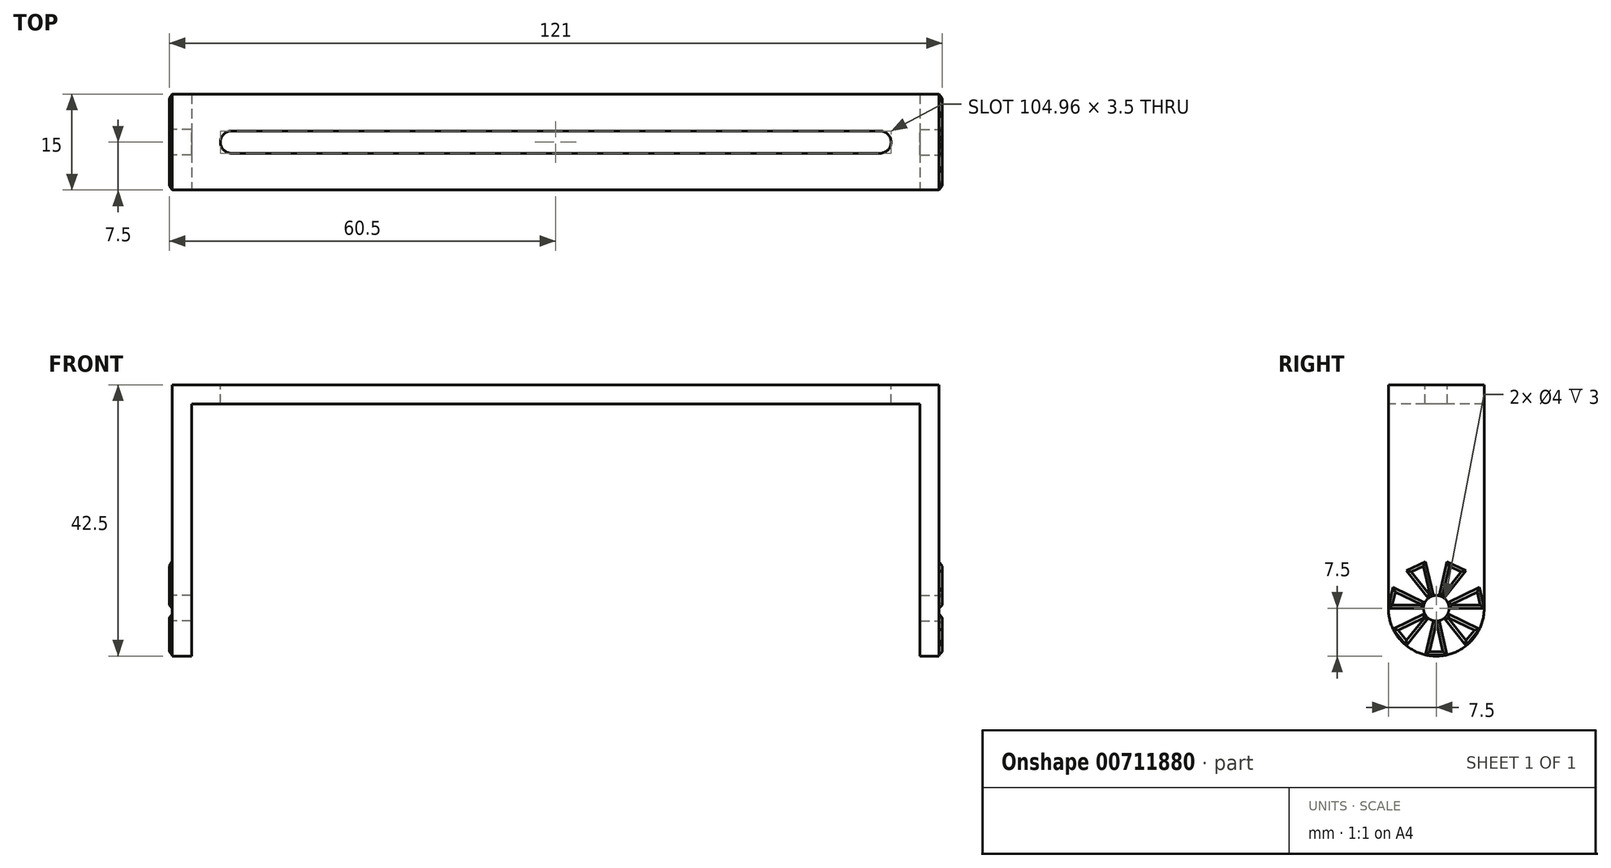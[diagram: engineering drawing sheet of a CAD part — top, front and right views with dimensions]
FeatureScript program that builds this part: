
annotation { "Feature Type Name" : "Feature", "Feature Type Description" : "" }
export const myFeature = defineFeature(function(context is Context, id is Id, definition is map)
    precondition{}
    {
        {
            var Q0;
            Q0=qCreatedBy(makeId("Top.planeOp"),FACE);
            var sketch = newSketch(context, id + "F0", { "sketchPlane" : qUnion([Q0])});
            skLineSegment(sketch, "E0", {"start": v(0, 7.5) * mm, "end": v(0, -7.5) * mm});
            skLineSegment(sketch, "E1", {"start": v(0, 7.5) * mm, "end": v(-60, 7.5) * mm});
            skLineSegment(sketch, "E2", {"start": v(-60, 7.5) * mm, "end": v(-60, -7.5) * mm});
            skLineSegment(sketch, "E3", {"start": v(0, -7.5) * mm, "end": v(-60, -7.5) * mm});
            skLineSegment(sketch, "E4", {"start": v(-57, 7.5) * mm, "end": v(-57, -7.5) * mm});
            skLineSegment(sketch, "E5.trimOffspring", {"start": v(-55, 0) * mm, "end": v(-50.73, 0) * mm});
            skPoint(sketch, "E6.start.orphan", {"position": v(-60, 0) * mm});
            skPoint(sketch, "E7.end.orphan", {"position": v(0, -3.5) * mm});
            skPoint(sketch, "E7.start.orphan", {"position": v(-60.73, -3.5) * mm});
            skPoint(sketch, "E8.end.orphan", {"position": v(-60.8, -3.5) * mm});
            skPoint(sketch, "E9.end.orphan", {"position": v(0, 3.5) * mm});
            skLineSegment(sketch, "E10", {"start": v(-50.73, 0) * mm, "end": v(0, 0) * mm});
            skPoint(sketch, "E11.orphan", {"position": v(-57, 0) * mm});
            skArc(sketch, "E12.0.startCap", {"start": v(-50.73, -1.75) * mm, "mid": v(-52.48, 0) * mm, "end": v(-50.73, 1.75) * mm});
            skLineSegment(sketch, "E12.0.left", {"start": v(-50.73, 1.75) * mm, "end": v(10, 1.75) * mm});
            skLineSegment(sketch, "E12.0.right", {"start": v(-50.73, -1.75) * mm, "end": v(10, -1.75) * mm});
            skSolve(sketch);
        }
        {
            var Q0;
            {var subQ0=sQuery(id+"F0.wireOp",EDGE,"E2");Q0=makeQuery(id+"F0.imprint","IMPRINT",FACE,{"disambiguationData":[TD([[makeQuery(id+"F0.imprint","IMPRINT",EDGE,{"derivedFrom":subQ0}),1.0]])]});}
            extrude(context, id + "F1", {"entities" : qUnion([Q0]), "oppositeDirection" : true, "depth" : 35 * mm, "offsetDistance" : 25 * mm});
        }
        {
            var Q0;
            {var subQ3=sQuery(id+"F0.wireOp",EDGE,"E4");Q0=makeQuery(id+"F0.imprint","IMPRINT",FACE,{"disambiguationData":[TD([[makeQuery(id+"F0.imprint","IMPRINT",EDGE,{"derivedFrom":subQ3}),1.0]])]});}
            extrude(context, id + "F2", {"entities" : qUnion([Q0]), "operationType" : NewBodyOperationType.ADD, "oppositeDirection" : true, "depth" : 3 * mm, "offsetDistance" : 25 * mm});
        }
        {
            var Q0;
            Q0=makeQuery(id+"F1.opExtrude","CAP_FACE",FACE,{"disambiguationData":[OSD([sQuery(id+"F0.wireOp",EDGE,"E1"),sQuery(id+"F0.wireOp",EDGE,"E2"),sQuery(id+"F0.wireOp",EDGE,"E3"),sQuery(id+"F0.wireOp",EDGE,"E4")])],"isStart":false});
            var sketch = newSketch(context, id + "F3", { "sketchPlane" : qUnion([Q0])});
            skLineSegment(sketch, "E13", {"start": v(-74.84, 0) * mm, "end": v(-34.44, 0) * mm});
            skPoint(sketch, "E13.startSnap0", {"position": v(-60, 0) * mm});
            skSolve(sketch);
        }
        {
            var Q0;
            {var subQ5=makeQuery(id+"F1.opExtrude","CAP_EDGE",EDGE,{"disambiguationData":[OSD([sQuery(id+"F0.wireOp",EDGE,"E3")])],"isStart":false});Q0=makeQuery(id+"F3.imprint","IMPRINT",FACE,{"disambiguationData":[TD([[makeQuery(id+"F3.imprint","IMPRINT",EDGE,{"derivedFrom":subQ5}),1.0]])]});}
            var Q1;
            Q1=sQuery(id+"F3.wireOp",EDGE,"E13");
            revolve(context, id + "F4", {"operationType" : NewBodyOperationType.ADD, "surfaceOperationType" : NewSurfaceOperationType.NEW, "entities" : qUnion([Q0]), "axis" : qUnion([Q1]), "revolveType" : RevolveType.FULL});
        }
        {
            var Q0;
            {var subQ0=sQuery(id+"F0.wireOp",EDGE,"E2");Q0=makeQuery(id+"F4.boolean.opBoolean","MERGE",FACE,{"derivedFrom":[makeQuery(id+"F1.opExtrude","SWEPT_FACE",FACE,{"disambiguationData":[OSD([subQ0])]}),makeQuery(id+"F4.opRevolve","SWEPT_FACE",FACE,{"disambiguationData":[OSD([subQ0])]})]});}
            var sketch = newSketch(context, id + "F5", { "sketchPlane" : qUnion([Q0])});
            skCircle(sketch, "E14", {"center": v(0, -35) * mm, "radius": 7.5 * mm});
            skCircle(sketch, "E15", {"center": v(0, -35) * mm, "radius": 2 * mm});
            skCircle(sketch, "E16.cCircle", {"center": v(0, -35) * mm, "radius": 7.5 * mm, "construction": true});
            skLineSegment(sketch, "E16.0", {"start": v(7.5, -35) * mm, "end": v(6.76, -38.25) * mm});
            skLineSegment(sketch, "E16.1", {"start": v(6.76, -38.25) * mm, "end": v(4.68, -40.86) * mm});
            skLineSegment(sketch, "E16.2", {"start": v(4.68, -40.86) * mm, "end": v(1.67, -42.31) * mm});
            skLineSegment(sketch, "E16.3", {"start": v(1.67, -42.31) * mm, "end": v(-1.67, -42.31) * mm});
            skLineSegment(sketch, "E16.4", {"start": v(-1.67, -42.31) * mm, "end": v(-4.68, -40.86) * mm});
            skLineSegment(sketch, "E16.5", {"start": v(-4.68, -40.86) * mm, "end": v(-6.76, -38.25) * mm});
            skLineSegment(sketch, "E16.6", {"start": v(-6.76, -38.25) * mm, "end": v(-7.5, -35) * mm});
            skLineSegment(sketch, "E16.7", {"start": v(-7.5, -35) * mm, "end": v(-6.76, -31.75) * mm});
            skLineSegment(sketch, "E16.8", {"start": v(-6.76, -31.75) * mm, "end": v(-4.68, -29.14) * mm});
            skLineSegment(sketch, "E16.9", {"start": v(-4.68, -29.14) * mm, "end": v(-1.67, -27.69) * mm});
            skLineSegment(sketch, "E16.10", {"start": v(-1.67, -27.69) * mm, "end": v(1.67, -27.69) * mm});
            skLineSegment(sketch, "E16.11", {"start": v(1.67, -27.69) * mm, "end": v(4.68, -29.14) * mm});
            skLineSegment(sketch, "E16.12", {"start": v(4.68, -29.14) * mm, "end": v(6.76, -31.75) * mm});
            skLineSegment(sketch, "E16.13", {"start": v(6.76, -31.75) * mm, "end": v(7.5, -35) * mm});
            skLineSegment(sketch, "E17", {"start": v(7.5, -35) * mm, "end": v(2, -35) * mm});
            skLineSegment(sketch, "E18", {"start": v(6.76, -31.75) * mm, "end": v(1.8, -34.13) * mm});
            skLineSegment(sketch, "E19", {"start": v(4.68, -29.14) * mm, "end": v(1.25, -33.44) * mm});
            skLineSegment(sketch, "E20", {"start": v(1.67, -27.69) * mm, "end": v(0.45, -33.05) * mm});
            skLineSegment(sketch, "E21", {"start": v(-1.67, -27.69) * mm, "end": v(-0.45, -33.05) * mm});
            skLineSegment(sketch, "E22", {"start": v(-4.68, -29.14) * mm, "end": v(-1.25, -33.44) * mm});
            skLineSegment(sketch, "E23", {"start": v(6.76, -38.25) * mm, "end": v(1.8, -35.87) * mm});
            skLineSegment(sketch, "E24.trimOffspring", {"start": v(-0.45, -36.95) * mm, "end": v(-1.67, -42.31) * mm});
            skLineSegment(sketch, "E25.trimOffspring", {"start": v(0.45, -36.95) * mm, "end": v(1.67, -42.31) * mm});
            skLineSegment(sketch, "E26.trimOffspring", {"start": v(1.25, -36.56) * mm, "end": v(4.68, -40.86) * mm});
            skLineSegment(sketch, "E27.trimOffspring", {"start": v(-1.8, -34.13) * mm, "end": v(-6.76, -31.75) * mm});
            skLineSegment(sketch, "E28.trimOffspring", {"start": v(-2, -35) * mm, "end": v(-7.5, -35) * mm});
            skLineSegment(sketch, "E29.trimOffspring", {"start": v(-1.8, -35.87) * mm, "end": v(-6.76, -38.25) * mm});
            skLineSegment(sketch, "E30.trimOffspring", {"start": v(-1.25, -36.56) * mm, "end": v(-4.68, -40.86) * mm});
            skSolve(sketch);
        }
        {
            var Q0;
            {var subQ5=sQuery(id+"F5.wireOp",EDGE,"E16.1");Q0=makeQuery(id+"F5.imprint","IMPRINT",FACE,{"disambiguationData":[TD([[makeQuery(id+"F5.imprint","IMPRINT",EDGE,{"derivedFrom":subQ5}),-1.0]])]});}
            var Q1;
            {var subQ5=sQuery(id+"F5.wireOp",EDGE,"E16.3");Q1=makeQuery(id+"F5.imprint","IMPRINT",FACE,{"disambiguationData":[TD([[makeQuery(id+"F5.imprint","IMPRINT",EDGE,{"derivedFrom":subQ5}),-1.0]])]});}
            var Q2;
            {var subQ5=sQuery(id+"F5.wireOp",EDGE,"E16.5");Q2=makeQuery(id+"F5.imprint","IMPRINT",FACE,{"disambiguationData":[TD([[makeQuery(id+"F5.imprint","IMPRINT",EDGE,{"derivedFrom":subQ5}),-1.0]])]});}
            var Q3;
            {var subQ5=sQuery(id+"F5.wireOp",EDGE,"E16.7");Q3=makeQuery(id+"F5.imprint","IMPRINT",FACE,{"disambiguationData":[TD([[makeQuery(id+"F5.imprint","IMPRINT",EDGE,{"derivedFrom":subQ5}),-1.0]])]});}
            var Q4;
            {var subQ5=sQuery(id+"F5.wireOp",EDGE,"E16.9");Q4=makeQuery(id+"F5.imprint","IMPRINT",FACE,{"disambiguationData":[TD([[makeQuery(id+"F5.imprint","IMPRINT",EDGE,{"derivedFrom":subQ5}),-1.0]])]});}
            var Q5;
            {var subQ5=sQuery(id+"F5.wireOp",EDGE,"E16.11");Q5=makeQuery(id+"F5.imprint","IMPRINT",FACE,{"disambiguationData":[TD([[makeQuery(id+"F5.imprint","IMPRINT",EDGE,{"derivedFrom":subQ5}),-1.0]])]});}
            var Q6;
            {var subQ5=sQuery(id+"F5.wireOp",EDGE,"E16.13");Q6=makeQuery(id+"F5.imprint","IMPRINT",FACE,{"disambiguationData":[TD([[makeQuery(id+"F5.imprint","IMPRINT",EDGE,{"derivedFrom":subQ5}),-1.0]])]});}
            extrude(context, id + "F6", {"entities" : qUnion([Q0, Q1, Q2, Q3, Q4, Q5, Q6]), "operationType" : NewBodyOperationType.ADD, "depth" : 0.5 * mm, "offsetDistance" : 25 * mm, "hasDraft" : true, "draftAngle" : 45 * degree, "draftPullDirection" : true});
        }
        {
            var Q0;
            {var subQ0=sQuery(id+"F5.wireOp",EDGE,"E15");var subQ8=makeQuery(id+"F5.imprint","INTERSECT",VERTEX,{"derivedFrom":[subQ0,sQuery(id+"F5.wireOp",EDGE,"E17")]});Q0=makeQuery(id+"F5.imprint","IMPRINT",FACE,{"disambiguationData":[TD([[makeQuery(id+"F5.imprint","IMPRINT",EDGE,{"disambiguationData":[TD([[subQ8,-1.0]])],"derivedFrom":subQ0}),1.0]])]});}
            extrude(context, id + "F7", {"entities" : qUnion([Q0]), "operationType" : NewBodyOperationType.REMOVE, "oppositeDirection" : true, "depth" : 25 * mm, "offsetDistance" : 25 * mm});
        }
        {
            var Q0;
            Q0=makeQuery(id+"F1.opExtrude","SWEPT_BODY",BODY,{"disambiguationData":[OSD([sQuery(id+"F0.wireOp",EDGE,"E1"),sQuery(id+"F0.wireOp",EDGE,"E2"),sQuery(id+"F0.wireOp",EDGE,"E3"),sQuery(id+"F0.wireOp",EDGE,"E4")])]});
            var Q1;
            Q1=qCreatedBy(makeId("Right.planeOp"),FACE);
            mirror(context, id + "F8", {"operationType" : NewBodyOperationType.ADD, "entities" : qUnion([Q0]), "mirrorPlane" : qUnion([Q1])});
        }
    });
